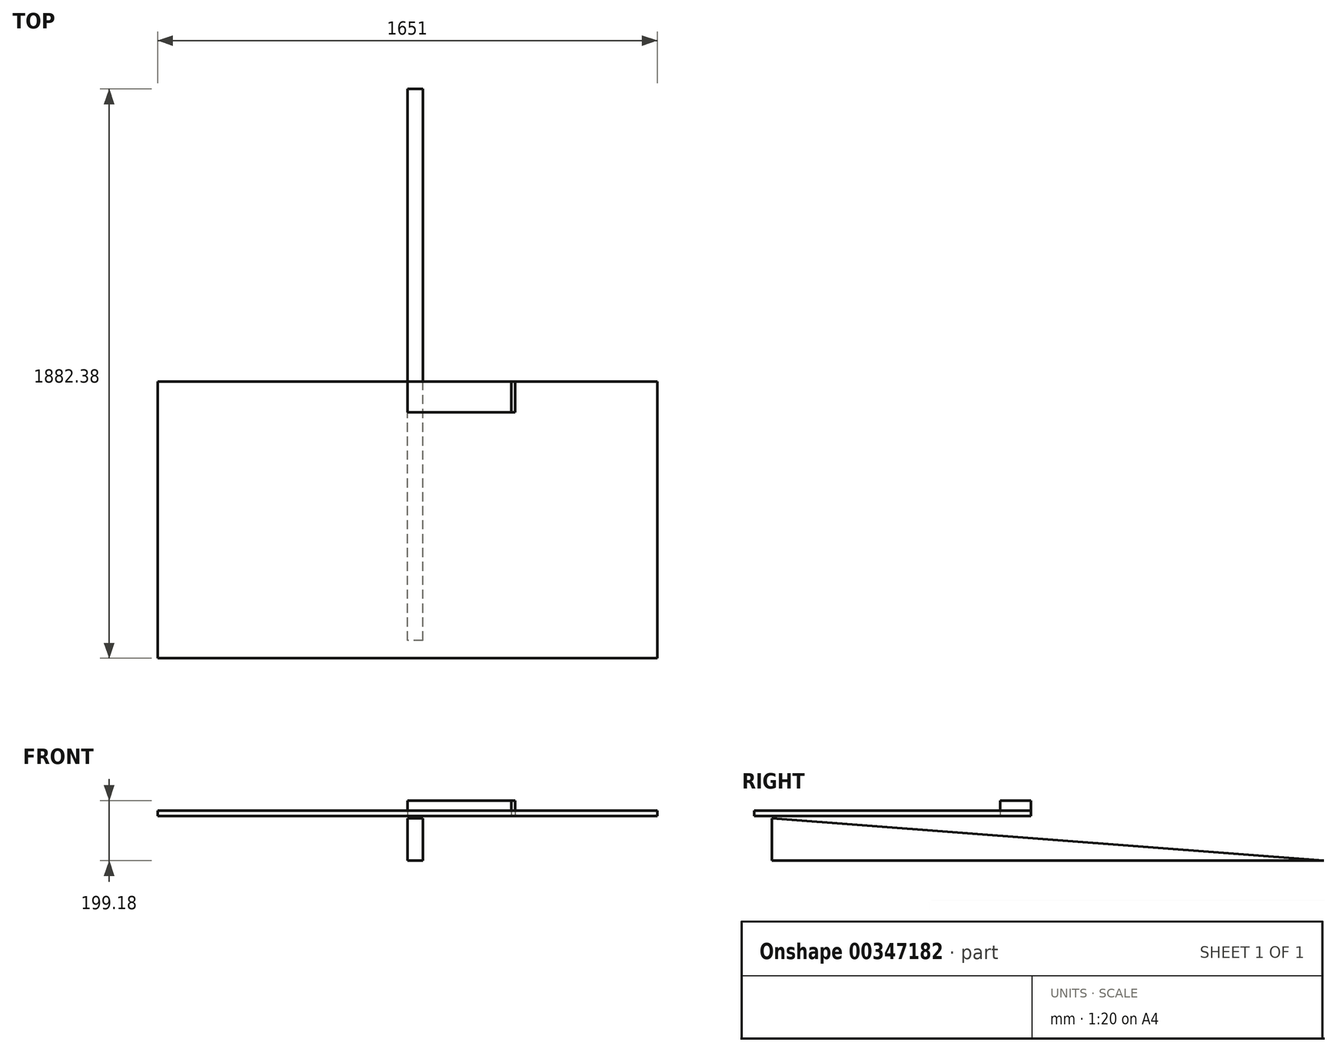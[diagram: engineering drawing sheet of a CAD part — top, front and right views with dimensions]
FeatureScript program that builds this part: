
annotation { "Feature Type Name" : "Feature", "Feature Type Description" : "" }
export const myFeature = defineFeature(function(context is Context, id is Id, definition is map)
    precondition{}
    {
        {
            var Q0;
            Q0=qCreatedBy(makeId("Right.planeOp"),FACE);
            var sketch = newSketch(context, id + "F0", { "sketchPlane" : qUnion([Q0])});
            skLineSegment(sketch, "E0.bottom", {"start": v(-914.4, 16.97) * mm, "end": v(0, 16.97) * mm});
            skLineSegment(sketch, "E0.top", {"start": v(-914.4, 0) * mm, "end": v(0, 0) * mm});
            skLineSegment(sketch, "E0.left", {"start": v(-914.4, 16.97) * mm, "end": v(-914.4, 0) * mm});
            skLineSegment(sketch, "E0.right", {"start": v(0, 16.97) * mm, "end": v(0, 0) * mm});
            skSolve(sketch);
        }
        {
            var Q0;
            Q0 = qSketchRegion(id + "F0", true);
            extrude(context, id + "F1", {"entities" : qUnion([Q0]), "endBound" : BoundingType.SYMMETRIC, "depth" : 1651 * mm});
        }
        {
            var Q0;
            Q0=qCreatedBy(makeId("Right.planeOp"),FACE);
            var sketch = newSketch(context, id + "F2", { "sketchPlane" : qUnion([Q0])});
            skLineSegment(sketch, "E1", {"start": v(-855.48, -8.68) * mm, "end": v(-855.48, -148.38) * mm});
            skLineSegment(sketch, "E2", {"start": v(-855.48, -148.38) * mm, "end": v(967.98, -148.38) * mm});
            skLineSegment(sketch, "E3", {"start": v(-855.48, -8.68) * mm, "end": v(967.98, -148.38) * mm});
            skSolve(sketch);
        }
        {
            var Q0;
            Q0 = qSketchRegion(id + "F2", true);
            extrude(context, id + "F3", {"entities" : qUnion([Q0]), "depth" : 50.8 * mm});
        }
        {
            var Q0;
            Q0=qCreatedBy(makeId("Right.planeOp"),FACE);
            var sketch = newSketch(context, id + "F4", { "sketchPlane" : qUnion([Q0])});
            skLineSegment(sketch, "E4.bottom", {"start": v(-101.6, 50.8) * mm, "end": v(0, 50.8) * mm});
            skLineSegment(sketch, "E4.top", {"start": v(-101.6, 0) * mm, "end": v(0, 0) * mm});
            skLineSegment(sketch, "E4.left", {"start": v(-101.6, 50.8) * mm, "end": v(-101.6, 0) * mm});
            skLineSegment(sketch, "E4.right", {"start": v(0, 50.8) * mm, "end": v(0, 0) * mm});
            skSolve(sketch);
        }
        {
            var Q0;
            Q0=makeQuery(id+"F4.imprint","IMPRINT",FACE,{"disambiguationData":[TD([[makeQuery(id+"F4.imprint","IMPRINT",EDGE,{"derivedFrom":sQuery(id+"F4.wireOp",EDGE,"E4.bottom")}),-1.0]])]});
            extrude(context, id + "F5", {"entities" : qUnion([Q0]), "depth" : 342.9 * mm});
        }
        {
            var Q0;
            Q0=qCreatedBy(makeId("Right.planeOp"),FACE);
            var sketch = newSketch(context, id + "F6", { "sketchPlane" : qUnion([Q0])});
            skLineSegment(sketch, "E5.bottom", {"start": v(-101.6, 50.8) * mm, "end": v(0, 50.8) * mm});
            skLineSegment(sketch, "E5.top", {"start": v(-101.6, 0) * mm, "end": v(0, 0) * mm});
            skLineSegment(sketch, "E5.left", {"start": v(-101.6, 50.8) * mm, "end": v(-101.6, 0) * mm});
            skLineSegment(sketch, "E5.right", {"start": v(0, 50.8) * mm, "end": v(0, 0) * mm});
            skSolve(sketch);
        }
        {
            var Q0;
            Q0 = qSketchRegion(id + "F6", true);
            extrude(context, id + "F7", {"entities" : qUnion([Q0]), "depth" : 355.6 * mm});
        }
    });
